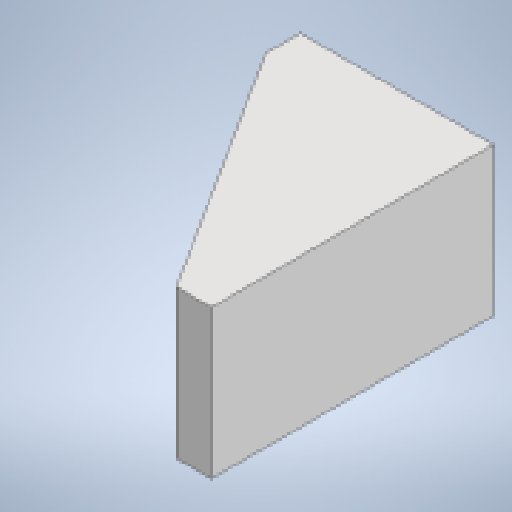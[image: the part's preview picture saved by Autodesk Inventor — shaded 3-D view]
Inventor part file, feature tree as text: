
AUTODESK INVENTOR PART (.ipt)
format: ipt  version: 2025.2 (Build 292293000, 293)  size: 159,232 bytes
history: native  units: mm
features: reference x14, extrude x4, sketch x4, other x4, thread x2, plane x1
ambient origin geometry x8: Origin, YZ Plane, XZ Plane, XY Plane, X Axis, Y Axis, Z Axis, Center Point
bodies: Solid1 (feature_tree)
feature tree (29):
  extrude  "Extrusion1"  Depth=63.5mm TaperAngle=0.0deg
  plane  "Work Plane5"
  extrude  "Extrusion9"  Depth=19.05mm
  extrude  "Extrusion10"  Depth=10.0mm
  extrude  "Extrusion11"  [1 undecoded]
  sketch  "Sketch1"  dims[d0=10.0mm d1=63.5mm d2=0.0mm]
  reference  "Reference1"
  reference  "Reference2"
  sketch  "Sketch9"  dims[d19=19.05mm d20=0.0mm d21=12.7mm]
  sketch  "Sketch10"  dims[d22=0.0mm d23=0.0mm d24=10.0mm]
  reference  "Reference15"
  reference  "Reference16"
  reference  "Reference17"
  reference  "Reference18"
  reference  "Reference19"
  reference  "Reference20"
  sketch  "Sketch11"  dims[d25=0.0mm d26=0.0mm]
  reference  "Reference21"
  reference  "Reference22"
  reference  "Reference23"
  reference  "Reference24"
  reference  "Reference25"
  reference  "Reference26"
  parser-record x1  (decoder bookkeeping rows leaked as tree rows — omitted from the tree; the rows remain in map.json)
  other  "Y_Mount_V2.iam"
  other  "L_Channel:1"
  thread  "Threaded_Rod:2"  [1 undecoded]
  thread  "Threaded_Rod:1"  [1 undecoded]
  other  "3x6_Bar:1"
note: 3 required parameter values undecoded (feature->parameter linkage not recoverable at this tier; creation-order binding heuristic only, values carry confidence <= 0.55)
note: 1 file-system path scrubbed to <path> (originals preserved in map.json)
